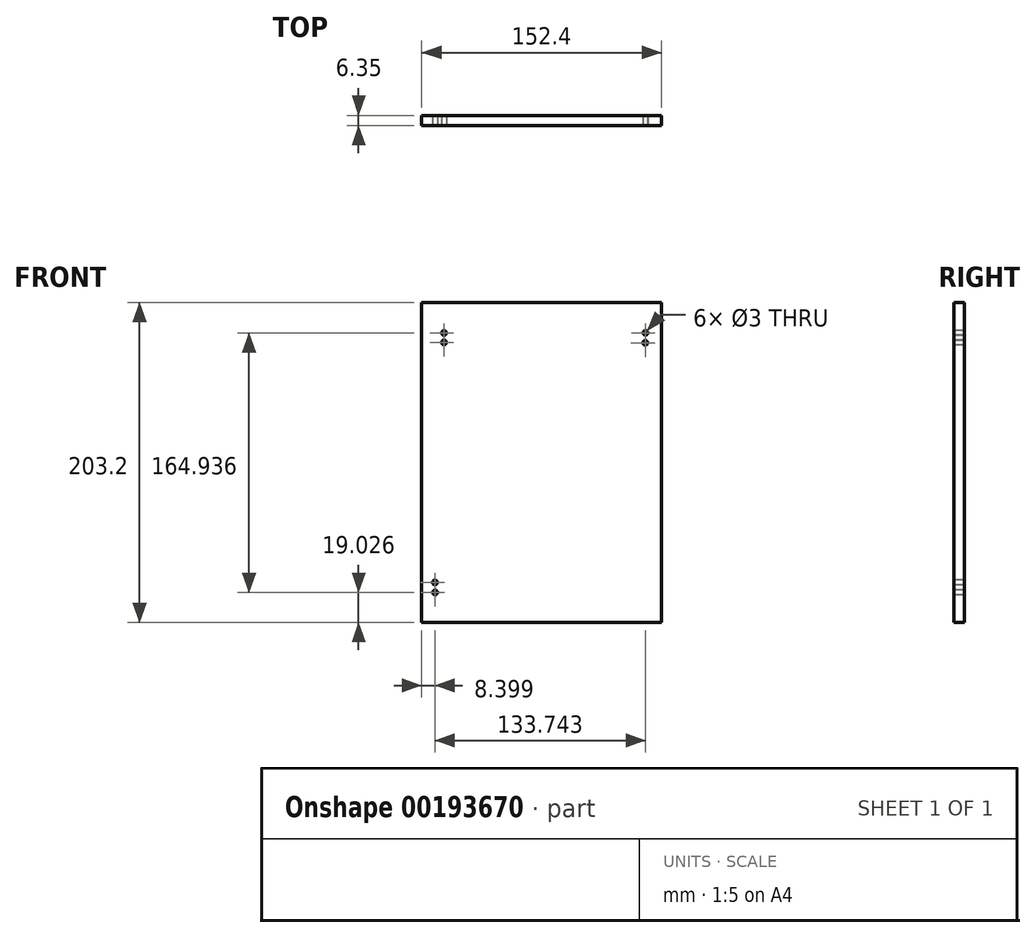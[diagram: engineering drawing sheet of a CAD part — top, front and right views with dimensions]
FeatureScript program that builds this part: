
annotation { "Feature Type Name" : "Feature", "Feature Type Description" : "" }
export const myFeature = defineFeature(function(context is Context, id is Id, definition is map)
    precondition{}
    {
        {
            var Q0;
            Q0=qCreatedBy(makeId("Front.planeOp"),FACE);
            var sketch = newSketch(context, id + "F0", { "sketchPlane" : qUnion([Q0])});
            skLineSegment(sketch, "E0.bottom", {"start": v(-76.2, 101.6) * mm, "end": v(76.2, 101.6) * mm});
            skLineSegment(sketch, "E0.top", {"start": v(-76.2, -101.6) * mm, "end": v(76.2, -101.6) * mm});
            skLineSegment(sketch, "E0.left", {"start": v(-76.2, 101.6) * mm, "end": v(-76.2, -101.6) * mm});
            skLineSegment(sketch, "E0.right", {"start": v(76.2, 101.6) * mm, "end": v(76.2, -101.6) * mm});
            skPoint(sketch, "E0.middle", {"position": v(0, 0) * mm});
            skSolve(sketch);
        }
        {
            var Q0;
            Q0=makeQuery(id+"F0.imprint","IMPRINT",FACE,{"disambiguationData":[TD([[makeQuery(id+"F0.imprint","IMPRINT",EDGE,{"derivedFrom":sQuery(id+"F0.wireOp",EDGE,"E0.bottom")}),-1.0]])]});
            extrude(context, id + "F1", {"entities" : qUnion([Q0]), "depth" : 6.35 * mm});
        }
        {
            var Q0;
            Q0=makeQuery(id+"F1.opExtrude","CAP_FACE",FACE,{"disambiguationData":[OSD([sQuery(id+"F0.wireOp",EDGE,"E0.bottom"),sQuery(id+"F0.wireOp",EDGE,"E0.top"),sQuery(id+"F0.wireOp",EDGE,"E0.left"),sQuery(id+"F0.wireOp",EDGE,"E0.right")])],"isStart":false});
            var sketch = newSketch(context, id + "F2", { "sketchPlane" : qUnion([Q0])});
            skLineSegment(sketch, "E1", {"start": v(-62.45, 101.6) * mm, "end": v(-62.45, 82.55) * mm});
            skLineSegment(sketch, "E2", {"start": v(-62.45, 82.55) * mm, "end": v(-62.45, 76.2) * mm});
            skSolve(sketch);
        }
        {
            var Q0;
            Q0=makeQuery(id+"F2.imprint","IMPRINT",FACE,{"disambiguationData":[TD([[makeQuery(id+"F2.imprint","IMPRINT",EDGE,{"derivedFrom":makeQuery(id+"F1.opExtrude","CAP_EDGE",EDGE,{"disambiguationData":[OSD([sQuery(id+"F0.wireOp",EDGE,"E0.top")])],"isStart":false})}),1.0]])]});
            var sketch = newSketch(context, id + "F3", { "sketchPlane" : qUnion([Q0])});
            skCircle(sketch, "E3", {"center": v(-62.05, 82.26) * mm, "radius": 1.5 * mm});
            skSolve(sketch);
        }
        {
            var Q0;
            Q0=makeQuery(id+"F2.imprint","IMPRINT",FACE,{"disambiguationData":[TD([[makeQuery(id+"F2.imprint","IMPRINT",EDGE,{"derivedFrom":makeQuery(id+"F1.opExtrude","CAP_EDGE",EDGE,{"disambiguationData":[OSD([sQuery(id+"F0.wireOp",EDGE,"E0.top")])],"isStart":false})}),1.0]])]});
            var sketch = newSketch(context, id + "F4", { "sketchPlane" : qUnion([Q0])});
            skCircle(sketch, "E4", {"center": v(-62.05, 76.26) * mm, "radius": 1.5 * mm});
            skSolve(sketch);
        }
        {
            var Q0;
            Q0 = qSketchRegion(id + "F3", true);
            extrude(context, id + "F5", {"entities" : qUnion([Q0]), "operationType" : NewBodyOperationType.REMOVE, "oppositeDirection" : true, "depth" : 6.35 * mm});
        }
        {
            var Q0;
            Q0 = qSketchRegion(id + "F4", true);
            var Q1;
            Q1=sQuery(id+"F4.wireOp",EDGE,"E4");
            extrude(context, id + "F6", {"entities" : qUnion([Q0]), "operationType" : NewBodyOperationType.REMOVE, "surfaceEntities" : qUnion([Q1]), "oppositeDirection" : true, "depth" : 6.35 * mm});
        }
        {
            var Q0;
            Q0=makeQuery(id+"F2.imprint","IMPRINT",FACE,{"disambiguationData":[TD([[makeQuery(id+"F2.imprint","IMPRINT",EDGE,{"derivedFrom":makeQuery(id+"F1.opExtrude","CAP_EDGE",EDGE,{"disambiguationData":[OSD([sQuery(id+"F0.wireOp",EDGE,"E0.top")])],"isStart":false})}),1.0]])]});
            var sketch = newSketch(context, id + "F7", { "sketchPlane" : qUnion([Q0])});
            skCircle(sketch, "E5", {"center": v(65.94, 82.36) * mm, "radius": 1.5 * mm});
            skCircle(sketch, "E6", {"center": v(65.86, 75.97) * mm, "radius": 1.5 * mm});
            skSolve(sketch);
        }
        {
            var Q0;
            Q0 = qSketchRegion(id + "F7", true);
            extrude(context, id + "F8", {"entities" : qUnion([Q0]), "operationType" : NewBodyOperationType.REMOVE, "oppositeDirection" : true, "depth" : 6.35 * mm});
        }
        {
            var Q0;
            Q0=makeQuery(id+"F2.imprint","IMPRINT",FACE,{"disambiguationData":[TD([[makeQuery(id+"F2.imprint","IMPRINT",EDGE,{"derivedFrom":makeQuery(id+"F1.opExtrude","CAP_EDGE",EDGE,{"disambiguationData":[OSD([sQuery(id+"F0.wireOp",EDGE,"E0.top")])],"isStart":false})}),1.0]])]});
            var sketch = newSketch(context, id + "F9", { "sketchPlane" : qUnion([Q0])});
            skCircle(sketch, "E7", {"center": v(-67.8, -76.2) * mm, "radius": 1.5 * mm});
            skSolve(sketch);
        }
        {
            var Q0;
            Q0=makeQuery(id+"F2.imprint","IMPRINT",FACE,{"disambiguationData":[TD([[makeQuery(id+"F2.imprint","IMPRINT",EDGE,{"derivedFrom":makeQuery(id+"F1.opExtrude","CAP_EDGE",EDGE,{"disambiguationData":[OSD([sQuery(id+"F0.wireOp",EDGE,"E0.top")])],"isStart":false})}),1.0]])]});
            var sketch = newSketch(context, id + "F10", { "sketchPlane" : qUnion([Q0])});
            skCircle(sketch, "E8", {"center": v(-67.66, -82.57) * mm, "radius": 1.5 * mm});
            skSolve(sketch);
        }
        {
            var Q0;
            Q0 = qSketchRegion(id + "F10", true);
            var Q1;
            Q1 = qSketchRegion(id + "F9", true);
            extrude(context, id + "F11", {"entities" : qUnion([Q0, Q1]), "operationType" : NewBodyOperationType.REMOVE, "oppositeDirection" : true, "depth" : 6.35 * mm});
        }
    });
